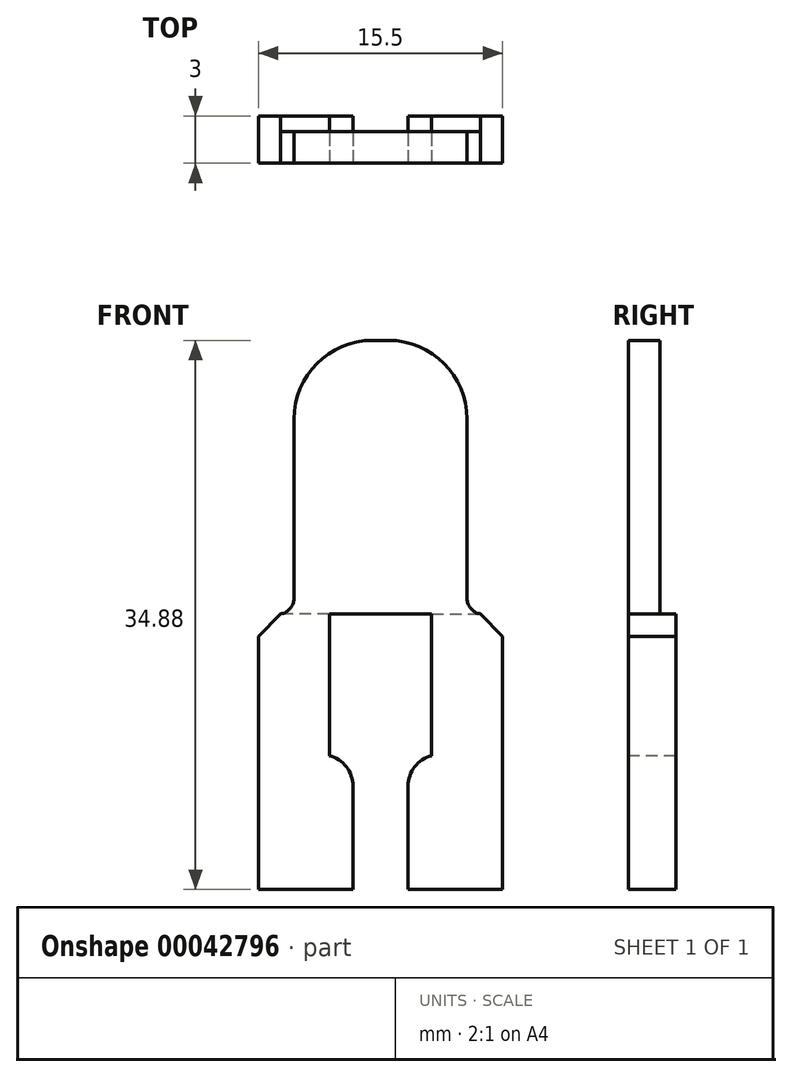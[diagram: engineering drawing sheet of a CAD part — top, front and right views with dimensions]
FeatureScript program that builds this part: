
annotation { "Feature Type Name" : "Feature", "Feature Type Description" : "" }
export const myFeature = defineFeature(function(context is Context, id is Id, definition is map)
    precondition{}
    {
        {
            var Q0;
            Q0=qCreatedBy(makeId("Top.planeOp"),FACE);
            var sketch = newSketch(context, id + "F0", { "sketchPlane" : qUnion([Q0])});
            skLineSegment(sketch, "E0.rect.bottom", {"start": v(10.12, -7.15) * mm, "end": v(-10.12, -7.15) * mm, "construction": true});
            skLineSegment(sketch, "E0.rect.top", {"start": v(5.82, 7.15) * mm, "end": v(-5.82, 7.15) * mm, "construction": true});
            skLineSegment(sketch, "E0.rect.left", {"start": v(10.12, -7.15) * mm, "end": v(10.12, 2.85) * mm, "construction": true});
            skLineSegment(sketch, "E0.rect.right", {"start": v(-10.12, -7.15) * mm, "end": v(-10.12, 2.85) * mm, "construction": true});
            skPoint(sketch, "E0.rect.middle", {"position": v(0, 0) * mm});
            skArc(sketch, "E1", {"start": v(-5.83, 7.15) * mm, "mid": v(-8.87, 5.9) * mm, "end": v(-10.13, 2.85) * mm, "construction": true});
            skLineSegment(sketch, "E2", {"start": v(0, -7.15) * mm, "end": v(0, 0) * mm, "construction": true});
            skLineSegment(sketch, "E3", {"start": v(10.12, 0) * mm, "end": v(0, 0) * mm, "construction": true});
            skArc(sketch, "E4.MirrorCS", {"start": v(5.82, 7.15) * mm, "mid": v(8.87, 5.9) * mm, "end": v(10.13, 2.85) * mm, "construction": true});
            skPoint(sketch, "E5.orphan", {"position": v(-10.12, 7.15) * mm});
            skPoint(sketch, "E6.orphan", {"position": v(10.12, 7.15) * mm});
            skLineSegment(sketch, "E7.rect.bottom", {"start": v(14, -12) * mm, "end": v(-14, -12) * mm});
            skLineSegment(sketch, "E7.rect.top", {"start": v(14, 12) * mm, "end": v(-14, 12) * mm});
            skLineSegment(sketch, "E7.rect.left", {"start": v(14, -12) * mm, "end": v(14, 12) * mm});
            skLineSegment(sketch, "E7.rect.right", {"start": v(-14, -12) * mm, "end": v(-14, 12) * mm});
            skSolve(sketch);
        }
        {
            var Q0;
            Q0=qCreatedBy(makeId("Front.planeOp"),FACE);
            var Q1;
            Q1=sQuery(id+"F0.wireOp",EDGE,"E7.rect.bottom");
            cPlane(context, id + "F1", {"entities" : qUnion([Q0, Q1]), "cplaneType" : CPlaneType.LINE_ANGLE, "offset" : 25 * mm, "angle" : 0 * degree, "width" : 150 * mm, "height" : 150 * mm});
        }
        {
            var Q0;
            Q0=qCreatedBy(id+"F1.planeOp",FACE);
            var sketch = newSketch(context, id + "F2", { "sketchPlane" : qUnion([Q0])});
            skLineSegment(sketch, "E8", {"start": v(0, 0) * mm, "end": v(0, 36.8) * mm, "construction": true});
            skLineSegment(sketch, "E9", {"start": v(-1.75, 0) * mm, "end": v(-7.75, 0) * mm});
            skLineSegment(sketch, "E10", {"start": v(-7.75, 0) * mm, "end": v(-7.75, 16.09) * mm});
            skLineSegment(sketch, "E11", {"start": v(-1.75, 0) * mm, "end": v(-1.75, 8.5) * mm});
            skLineSegment(sketch, "E12", {"start": v(-1.75, 8.5) * mm, "end": v(-3.25, 8.5) * mm});
            skLineSegment(sketch, "E13", {"start": v(-3.25, 8.5) * mm, "end": v(-3.25, 17.5) * mm});
            skLineSegment(sketch, "E14", {"start": v(-3.25, 17.5) * mm, "end": v(-6.34, 17.5) * mm});
            skLineSegment(sketch, "E15", {"start": v(-5.5, 17.5) * mm, "end": v(-5.5, 34.88) * mm});
            skLineSegment(sketch, "E16", {"start": v(-5.5, 34.88) * mm, "end": v(0, 34.88) * mm});
            skLineSegment(sketch, "E17.MirrorCS", {"start": v(3.25, 8.5) * mm, "end": v(3.25, 17.5) * mm});
            skLineSegment(sketch, "E18.MirrorCS", {"start": v(1.75, 0) * mm, "end": v(1.75, 8.5) * mm});
            skLineSegment(sketch, "E19.MirrorCS", {"start": v(1.75, 8.5) * mm, "end": v(3.25, 8.5) * mm});
            skLineSegment(sketch, "E20.MirrorCS", {"start": v(1.75, 0) * mm, "end": v(7.75, 0) * mm});
            skLineSegment(sketch, "E21.MirrorCS", {"start": v(7.75, 0) * mm, "end": v(7.75, 16.09) * mm});
            skLineSegment(sketch, "E22.MirrorCS", {"start": v(3.25, 17.5) * mm, "end": v(6.34, 17.5) * mm});
            skLineSegment(sketch, "E23.MirrorCS", {"start": v(5.5, 17.5) * mm, "end": v(5.5, 34.88) * mm});
            skLineSegment(sketch, "E24.MirrorCS", {"start": v(5.5, 34.88) * mm, "end": v(0, 34.88) * mm});
            skLineSegment(sketch, "E25", {"start": v(-6.34, 17.5) * mm, "end": v(-7.75, 16.09) * mm});
            skPoint(sketch, "E26.orphan", {"position": v(-7.75, 17.5) * mm});
            skLineSegment(sketch, "E27.MirrorCS", {"start": v(6.34, 17.5) * mm, "end": v(7.75, 16.09) * mm});
            skPoint(sketch, "E28.orphan", {"position": v(7.75, 17.5) * mm});
            skLineSegment(sketch, "E29", {"start": v(-3.25, 17.5) * mm, "end": v(3.25, 17.5) * mm});
            skSolve(sketch);
        }
        {
            var Q0;
            Q0=makeQuery(id+"F2.imprint","IMPRINT",FACE,{"disambiguationData":[TD([[makeQuery(id+"F2.imprint","IMPRINT",EDGE,{"derivedFrom":sQuery(id+"F2.wireOp",EDGE,"E9")}),-1.0]])]});
            var Q1;
            {var subQ0=sQuery(id+"F2.wireOp",EDGE,"E17.MirrorCS");Q1=makeQuery(id+"F2.imprint","IMPRINT",FACE,{"disambiguationData":[TD([[makeQuery(id+"F2.imprint","IMPRINT",EDGE,{"derivedFrom":subQ0}),-1.0]])]});}
            var Q2;
            {var subQ3=sQuery(id+"F2.wireOp",EDGE,"E15");Q2=makeQuery(id+"F2.imprint","IMPRINT",FACE,{"disambiguationData":[TD([[makeQuery(id+"F2.imprint","IMPRINT",EDGE,{"derivedFrom":subQ3}),-1.0]])]});}
            extrude(context, id + "F3", {"entities" : qUnion([Q0, Q1, Q2]), "depth" : 2 * mm, "offsetDistance" : 25 * mm});
        }
        {
            var Q0;
            Q0=makeQuery(id+"F3.opExtrude","SWEPT_FACE",FACE,{"disambiguationData":[OSD([sQuery(id+"F2.wireOp",EDGE,"E15")])]});
            var sketch = newSketch(context, id + "F4", { "sketchPlane" : qUnion([Q0])});
            skLineSegment(sketch, "E30.bottom", {"start": v(-11, 34.88) * mm, "end": v(-10, 34.88) * mm});
            skLineSegment(sketch, "E30.top", {"start": v(-11, 17.5) * mm, "end": v(-10, 17.5) * mm});
            skLineSegment(sketch, "E30.left", {"start": v(-11, 34.88) * mm, "end": v(-11, 17.5) * mm});
            skLineSegment(sketch, "E30.right", {"start": v(-10, 34.88) * mm, "end": v(-10, 17.5) * mm});
            skSolve(sketch);
        }
        {
            var Q0;
            Q0 = qSketchRegion(id + "F4", true);
            extrude(context, id + "F5", {"entities" : qUnion([Q0]), "operationType" : NewBodyOperationType.REMOVE, "endBound" : BoundingType.THROUGH_ALL, "oppositeDirection" : true, "depth" : 25 * mm, "offsetDistance" : 25 * mm});
        }
        {
            var Q0;
            Q0=makeQuery(id+"F3.opExtrude","SWEPT_EDGE",EDGE,{"disambiguationData":[OSD([sQuery(id+"F2.wireOp",EDGE,"E15"),sQuery(id+"F2.wireOp",EDGE,"E16")])]});
            var Q1;
            Q1=makeQuery(id+"F3.opExtrude","SWEPT_EDGE",EDGE,{"disambiguationData":[OSD([sQuery(id+"F2.wireOp",EDGE,"E23.MirrorCS"),sQuery(id+"F2.wireOp",EDGE,"E24.MirrorCS")])]});
            fillet(context, id + "F6", {"entities" : qUnion([Q0, Q1]), "tangentPropagation" : true, "radius" : 5 * mm, "defaultsChanged" : false, "vertexSettings" : [], "allowEdgeOverflow" : false});
        }
        {
            var Q0;
            Q0=makeQuery(id+"F3.opExtrude","SWEPT_EDGE",EDGE,{"disambiguationData":[OSD([sQuery(id+"F2.wireOp",EDGE,"E14"),sQuery(id+"F2.wireOp",EDGE,"E15")])]});
            var Q1;
            Q1=makeQuery(id+"F3.opExtrude","SWEPT_EDGE",EDGE,{"disambiguationData":[OSD([sQuery(id+"F2.wireOp",EDGE,"E22.MirrorCS"),sQuery(id+"F2.wireOp",EDGE,"E23.MirrorCS")])]});
            fillet(context, id + "F7", {"entities" : qUnion([Q0, Q1]), "tangentPropagation" : true, "radius" : 1 * mm, "defaultsChanged" : false, "vertexSettings" : [], "allowEdgeOverflow" : false});
        }
        {
            var Q0;
            Q0=makeQuery(id+"F3.opExtrude","SWEPT_EDGE",EDGE,{"disambiguationData":[OSD([sQuery(id+"F2.wireOp",EDGE,"E11"),sQuery(id+"F2.wireOp",EDGE,"E12")])]});
            var Q1;
            Q1=makeQuery(id+"F3.opExtrude","SWEPT_EDGE",EDGE,{"disambiguationData":[OSD([sQuery(id+"F2.wireOp",EDGE,"E18.MirrorCS"),sQuery(id+"F2.wireOp",EDGE,"E19.MirrorCS")])]});
            fillet(context, id + "F8", {"entities" : qUnion([Q0, Q1]), "tangentPropagation" : true, "radius" : 2 * mm, "defaultsChanged" : true, "vertexSettings" : [], "allowEdgeOverflow" : false});
        }
        {
            var Q0;
            Q0=makeQuery(id+"F3.opExtrude","CAP_FACE",FACE,{"disambiguationData":[OSD([sQuery(id+"F2.wireOp",EDGE,"E9"),sQuery(id+"F2.wireOp",EDGE,"E10"),sQuery(id+"F2.wireOp",EDGE,"E11"),sQuery(id+"F2.wireOp",EDGE,"E12"),sQuery(id+"F2.wireOp",EDGE,"E13"),sQuery(id+"F2.wireOp",EDGE,"E14"),sQuery(id+"F2.wireOp",EDGE,"E15"),sQuery(id+"F2.wireOp",EDGE,"E16"),sQuery(id+"F2.wireOp",EDGE,"E17.MirrorCS"),sQuery(id+"F2.wireOp",EDGE,"E18.MirrorCS"),sQuery(id+"F2.wireOp",EDGE,"E19.MirrorCS"),sQuery(id+"F2.wireOp",EDGE,"E20.MirrorCS"),sQuery(id+"F2.wireOp",EDGE,"E21.MirrorCS"),sQuery(id+"F2.wireOp",EDGE,"E22.MirrorCS"),sQuery(id+"F2.wireOp",EDGE,"E23.MirrorCS"),sQuery(id+"F2.wireOp",EDGE,"E24.MirrorCS"),sQuery(id+"F2.wireOp",EDGE,"E25"),sQuery(id+"F2.wireOp",EDGE,"E27.MirrorCS"),sQuery(id+"F2.wireOp",EDGE,"E29")])],"isStart":true});
            extrude(context, id + "F9", {"entities" : qUnion([Q0]), "operationType" : NewBodyOperationType.ADD, "depth" : 1 * mm, "offsetDistance" : 25 * mm});
        }
    });
